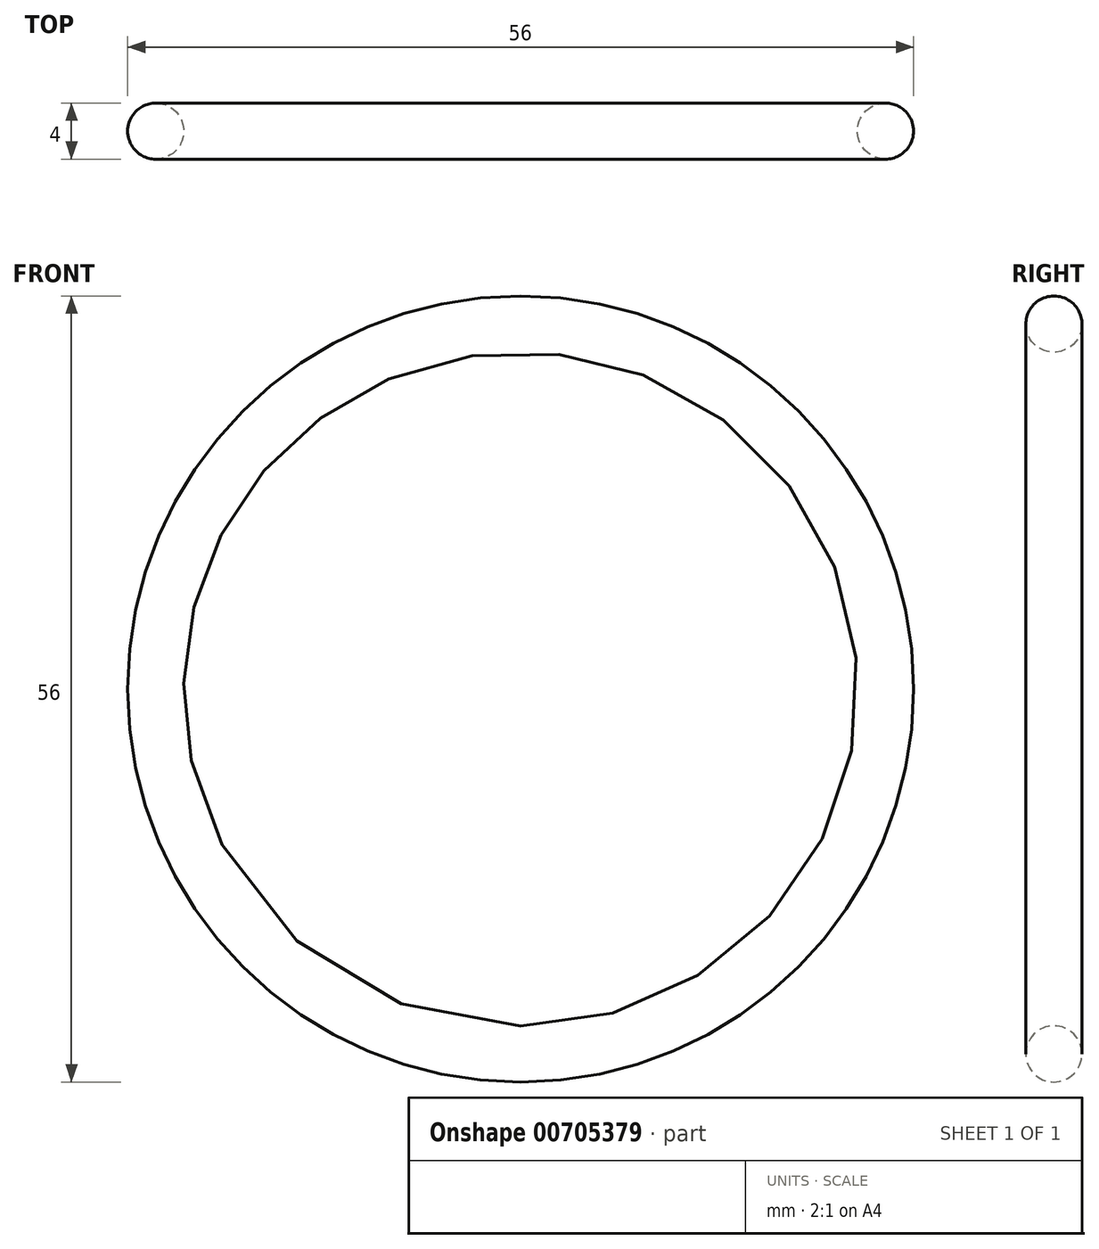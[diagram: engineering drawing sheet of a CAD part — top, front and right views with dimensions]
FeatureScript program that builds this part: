
annotation { "Feature Type Name" : "Feature", "Feature Type Description" : "" }
export const myFeature = defineFeature(function(context is Context, id is Id, definition is map)
    precondition{}
    {
        {
            var Q0;
            Q0=qCreatedBy(makeId("Right.planeOp"),FACE);
            var sketch = newSketch(context, id + "F0", { "sketchPlane" : qUnion([Q0])});
            skCircle(sketch, "E0", {"center": v(0, -26) * mm, "radius": 2 * mm});
            skSolve(sketch);
        }
        {
            var Q0;
            Q0=qCreatedBy(makeId("Right.planeOp"),FACE);
            var sketch = newSketch(context, id + "F1", { "sketchPlane" : qUnion([Q0])});
            skLineSegment(sketch, "E1", {"start": v(-46.44, 0) * mm, "end": v(51.25, 0) * mm, "construction": true});
            skSolve(sketch);
        }
        {
            var Q0;
            Q0=makeQuery(id+"F0.imprint","IMPRINT",FACE,{"disambiguationData":[TD([[makeQuery(id+"F0.imprint","IMPRINT",EDGE,{"derivedFrom":sQuery(id+"F0.wireOp",EDGE,"E0")}),1.0]])]});
            var Q1;
            Q1=sQuery(id+"F0.wireOp",EDGE,"E0");
            var Q2;
            Q2=sQuery(id+"F1.wireOp",EDGE,"E1");
            revolve(context, id + "F2", {"surfaceOperationType" : NewSurfaceOperationType.NEW, "entities" : qUnion([Q0]), "surfaceEntities" : qUnion([Q1]), "axis" : qUnion([Q2]), "revolveType" : RevolveType.FULL});
        }
    });
